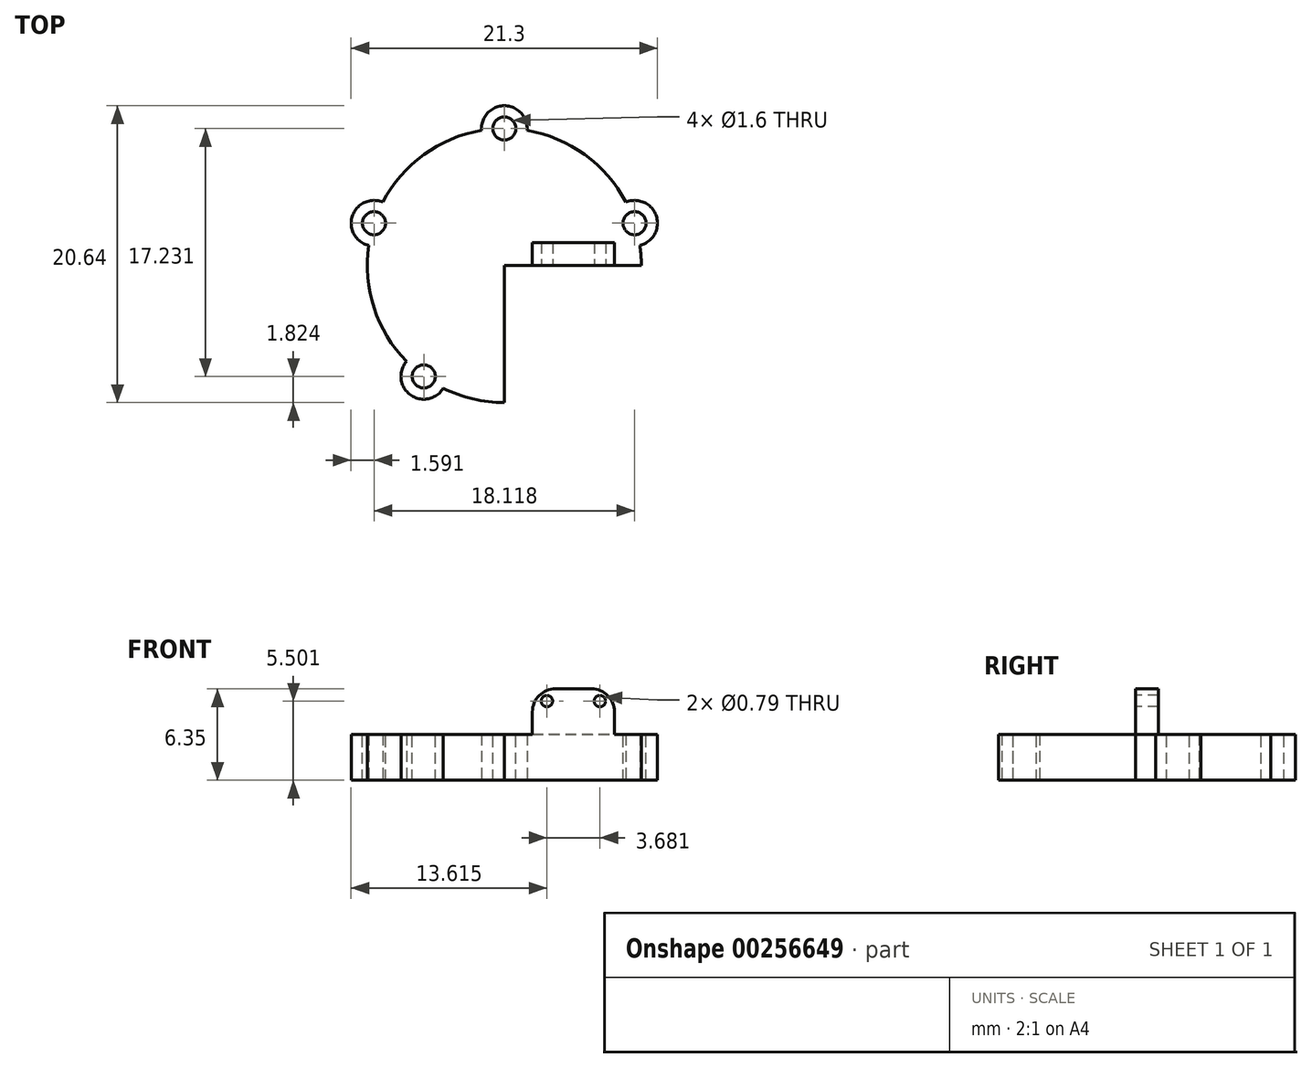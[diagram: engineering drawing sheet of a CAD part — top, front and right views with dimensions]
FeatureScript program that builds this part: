
annotation { "Feature Type Name" : "Feature", "Feature Type Description" : "" }
export const myFeature = defineFeature(function(context is Context, id is Id, definition is map)
    precondition{}
    {
        {
            var Q0;
            Q0=qCreatedBy(makeId("Top.planeOp"),FACE);
            var sketch = newSketch(context, id + "F0", { "sketchPlane" : qUnion([Q0])});
            skCircle(sketch, "E0", {"center": v(0, 0) * mm, "radius": 9.53 * mm});
            skSolve(sketch);
        }
        {
            var Q0;
            Q0=makeQuery(id+"F0.imprint","IMPRINT",FACE,{"disambiguationData":[TD([[makeQuery(id+"F0.imprint","IMPRINT",EDGE,{"derivedFrom":sQuery(id+"F0.wireOp",EDGE,"E0")}),1.0]])]});
            var sketch = newSketch(context, id + "F1", { "sketchPlane" : qUnion([Q0])});
            skCircle(sketch, "E1.0", {"center": v(0, 0) * mm, "radius": 9.53 * mm});
            skArc(sketch, "E2", {"start": v(1.58, 9.4) * mm, "mid": v(0, 11.11) * mm, "end": v(-1.58, 9.4) * mm});
            skCircle(sketch, "E3", {"center": v(0, 9.53) * mm, "radius": 0.8 * mm});
            skSolve(sketch);
        }
        {
            var Q0;
            Q0 = qSketchRegion(id + "F1", true);
            extrude(context, id + "F2", {"entities" : qUnion([Q0]), "depth" : 3.17 * mm});
        }
        {
            var Q0;
            Q0=qCreatedBy(makeId("Top.planeOp"),FACE);
            var sketch = newSketch(context, id + "F3", { "sketchPlane" : qUnion([Q0])});
            skArc(sketch, "E4.0", {"start": v(1.58, 9.4) * mm, "mid": v(0, 11.11) * mm, "end": v(-1.58, 9.4) * mm});
            skCircle(sketch, "E5.0", {"center": v(0, 9.53) * mm, "radius": 0.8 * mm});
            skArc(sketch, "E6.0", {"start": v(1.58, -9.4) * mm, "mid": v(0, 9.53) * mm, "end": v(-1.58, -9.4) * mm});
            skPoint(sketch, "E7.MirrorCS.end.orphan", {"position": v(-1.58, -9.4) * mm});
            skPoint(sketch, "E7.MirrorCS.start.orphan", {"position": v(1.58, -9.4) * mm});
            skArc(sketch, "E8.1.0", {"start": v(-8.44, 4.4) * mm, "mid": v(-10.57, 3.43) * mm, "end": v(-9.42, 1.4) * mm});
            skArc(sketch, "E8.2.0", {"start": v(-6.8, -6.67) * mm, "mid": v(-6.53, -9) * mm, "end": v(-4.24, -8.53) * mm});
            skArc(sketch, "E8.3.0", {"start": v(4.24, -8.53) * mm, "mid": v(6.53, -9) * mm, "end": v(6.8, -6.67) * mm});
            skArc(sketch, "E8.4.0", {"start": v(9.42, 1.4) * mm, "mid": v(10.57, 3.43) * mm, "end": v(8.44, 4.4) * mm});
            skCircle(sketch, "E9.1.0", {"center": v(-9.06, 2.94) * mm, "radius": 0.8 * mm});
            skCircle(sketch, "E9.2.0", {"center": v(-5.6, -7.7) * mm, "radius": 0.8 * mm});
            skCircle(sketch, "E9.3.0", {"center": v(5.6, -7.7) * mm, "radius": 0.8 * mm});
            skCircle(sketch, "E9.4.0", {"center": v(9.06, 2.94) * mm, "radius": 0.8 * mm});
            skSolve(sketch);
        }
        {
            var Q0;
            {var subQ0=sQuery(id+"F3.wireOp",EDGE,"E4.0");Q0=makeQuery(id+"F3.imprint","IMPRINT",FACE,{"disambiguationData":[TD([[makeQuery(id+"F3.imprint","IMPRINT",EDGE,{"derivedFrom":subQ0}),1.0]])]});}
            var Q1;
            {var subQ0=sQuery(id+"F3.wireOp",EDGE,"E6.0");var subQ1=sQuery(id+"F3.wireOp",EDGE,"E5.0");var subQ2=makeQuery(id+"F3.imprint","INTERSECT",VERTEX,{"disambiguationData":[OD(0.0)],"derivedFrom":[subQ1,subQ0]});Q1=makeQuery(id+"F3.imprint","IMPRINT",FACE,{"disambiguationData":[TD([[makeQuery(id+"F3.imprint","IMPRINT",EDGE,{"disambiguationData":[TD([[subQ2,1.0]])],"derivedFrom":subQ1}),1.0]])]});}
            var Q2;
            {var subQ0=sQuery(id+"F3.wireOp",EDGE,"E8.3.0");Q2=makeQuery(id+"F3.imprint","IMPRINT",FACE,{"disambiguationData":[TD([[makeQuery(id+"F3.imprint","IMPRINT",EDGE,{"derivedFrom":subQ0}),1.0]])]});}
            var Q3;
            {var subQ0=sQuery(id+"F3.wireOp",EDGE,"E9.3.0");var subQ1=sQuery(id+"F3.wireOp",EDGE,"E6.0");var subQ2=makeQuery(id+"F3.imprint","INTERSECT",VERTEX,{"disambiguationData":[OD(0.0)],"derivedFrom":[subQ1,subQ0]});Q3=makeQuery(id+"F3.imprint","IMPRINT",FACE,{"disambiguationData":[TD([[makeQuery(id+"F3.imprint","IMPRINT",EDGE,{"disambiguationData":[TD([[subQ2,-1.0]])],"derivedFrom":subQ1}),1.0]])]});}
            var Q4;
            {var subQ0=sQuery(id+"F3.wireOp",EDGE,"E8.4.0");Q4=makeQuery(id+"F3.imprint","IMPRINT",FACE,{"disambiguationData":[TD([[makeQuery(id+"F3.imprint","IMPRINT",EDGE,{"derivedFrom":subQ0}),1.0]])]});}
            var Q5;
            {var subQ0=sQuery(id+"F3.wireOp",EDGE,"E9.4.0");var subQ1=sQuery(id+"F3.wireOp",EDGE,"E6.0");var subQ2=makeQuery(id+"F3.imprint","INTERSECT",VERTEX,{"disambiguationData":[OD(0.0)],"derivedFrom":[subQ1,subQ0]});Q5=makeQuery(id+"F3.imprint","IMPRINT",FACE,{"disambiguationData":[TD([[makeQuery(id+"F3.imprint","IMPRINT",EDGE,{"disambiguationData":[TD([[subQ2,-1.0]])],"derivedFrom":subQ1}),1.0]])]});}
            var Q6;
            {var subQ0=sQuery(id+"F3.wireOp",EDGE,"E9.1.0");var subQ1=sQuery(id+"F3.wireOp",EDGE,"E6.0");var subQ2=makeQuery(id+"F3.imprint","INTERSECT",VERTEX,{"disambiguationData":[OD(0.0)],"derivedFrom":[subQ1,subQ0]});Q6=makeQuery(id+"F3.imprint","IMPRINT",FACE,{"disambiguationData":[TD([[makeQuery(id+"F3.imprint","IMPRINT",EDGE,{"disambiguationData":[TD([[subQ2,-1.0]])],"derivedFrom":subQ1}),1.0]])]});}
            var Q7;
            {var subQ0=sQuery(id+"F3.wireOp",EDGE,"E8.2.0");Q7=makeQuery(id+"F3.imprint","IMPRINT",FACE,{"disambiguationData":[TD([[makeQuery(id+"F3.imprint","IMPRINT",EDGE,{"derivedFrom":subQ0}),1.0]])]});}
            var Q8;
            {var subQ0=sQuery(id+"F3.wireOp",EDGE,"E9.2.0");var subQ1=sQuery(id+"F3.wireOp",EDGE,"E6.0");var subQ2=makeQuery(id+"F3.imprint","INTERSECT",VERTEX,{"disambiguationData":[OD(0.0)],"derivedFrom":[subQ1,subQ0]});Q8=makeQuery(id+"F3.imprint","IMPRINT",FACE,{"disambiguationData":[TD([[makeQuery(id+"F3.imprint","IMPRINT",EDGE,{"disambiguationData":[TD([[subQ2,-1.0]])],"derivedFrom":subQ1}),1.0]])]});}
            var Q9;
            {var subQ0=sQuery(id+"F3.wireOp",EDGE,"E6.0");var subQ1=sQuery(id+"F3.wireOp",EDGE,"E5.0");var subQ2=makeQuery(id+"F3.imprint","INTERSECT",VERTEX,{"disambiguationData":[OD(0.0)],"derivedFrom":[subQ1,subQ0]});Q9=makeQuery(id+"F3.imprint","IMPRINT",FACE,{"disambiguationData":[TD([[makeQuery(id+"F3.imprint","IMPRINT",EDGE,{"disambiguationData":[TD([[subQ2,-1.0]])],"derivedFrom":subQ1}),1.0]])]});}
            var Q10;
            {var subQ0=sQuery(id+"F3.wireOp",EDGE,"E9.3.0");var subQ1=sQuery(id+"F3.wireOp",EDGE,"E6.0");var subQ2=makeQuery(id+"F3.imprint","INTERSECT",VERTEX,{"disambiguationData":[OD(0.0)],"derivedFrom":[subQ1,subQ0]});Q10=makeQuery(id+"F3.imprint","IMPRINT",FACE,{"disambiguationData":[TD([[makeQuery(id+"F3.imprint","IMPRINT",EDGE,{"disambiguationData":[TD([[subQ2,-1.0]])],"derivedFrom":subQ1}),-1.0]])]});}
            var Q11;
            {var subQ0=sQuery(id+"F3.wireOp",EDGE,"E9.4.0");var subQ1=sQuery(id+"F3.wireOp",EDGE,"E6.0");var subQ2=makeQuery(id+"F3.imprint","INTERSECT",VERTEX,{"disambiguationData":[OD(0.0)],"derivedFrom":[subQ1,subQ0]});Q11=makeQuery(id+"F3.imprint","IMPRINT",FACE,{"disambiguationData":[TD([[makeQuery(id+"F3.imprint","IMPRINT",EDGE,{"disambiguationData":[TD([[subQ2,-1.0]])],"derivedFrom":subQ1}),-1.0]])]});}
            var Q12;
            {var subQ0=sQuery(id+"F3.wireOp",EDGE,"E9.1.0");var subQ1=sQuery(id+"F3.wireOp",EDGE,"E6.0");var subQ2=makeQuery(id+"F3.imprint","INTERSECT",VERTEX,{"disambiguationData":[OD(0.0)],"derivedFrom":[subQ1,subQ0]});Q12=makeQuery(id+"F3.imprint","IMPRINT",FACE,{"disambiguationData":[TD([[makeQuery(id+"F3.imprint","IMPRINT",EDGE,{"disambiguationData":[TD([[subQ2,-1.0]])],"derivedFrom":subQ1}),-1.0]])]});}
            var Q13;
            {var subQ0=sQuery(id+"F3.wireOp",EDGE,"E9.2.0");var subQ1=sQuery(id+"F3.wireOp",EDGE,"E6.0");var subQ2=makeQuery(id+"F3.imprint","INTERSECT",VERTEX,{"disambiguationData":[OD(0.0)],"derivedFrom":[subQ1,subQ0]});Q13=makeQuery(id+"F3.imprint","IMPRINT",FACE,{"disambiguationData":[TD([[makeQuery(id+"F3.imprint","IMPRINT",EDGE,{"disambiguationData":[TD([[subQ2,-1.0]])],"derivedFrom":subQ1}),-1.0]])]});}
            var Q14;
            {var subQ0=sQuery(id+"F3.wireOp",EDGE,"E8.1.0");Q14=makeQuery(id+"F3.imprint","IMPRINT",FACE,{"disambiguationData":[TD([[makeQuery(id+"F3.imprint","IMPRINT",EDGE,{"derivedFrom":subQ0}),1.0]])]});}
            extrude(context, id + "F4", {"entities" : qUnion([Q0, Q1, Q2, Q3, Q4, Q5, Q6, Q7, Q8, Q9, Q10, Q11, Q12, Q13, Q14]), "operationType" : NewBodyOperationType.ADD, "depth" : 3.17 * mm});
        }
        {
            var Q0;
            {var subQ0=sQuery(id+"F3.wireOp",EDGE,"E6.0");Q0=makeQuery(id+"F4.boolean.opBoolean","MERGE",FACE,{"derivedFrom":[makeQuery(id+"F2.opExtrude","CAP_FACE",FACE,{"disambiguationData":[OSD([sQuery(id+"F1.wireOp",EDGE,"E1.0"),sQuery(id+"F1.wireOp",EDGE,"E2"),sQuery(id+"F1.wireOp",EDGE,"E3")])],"isStart":false}),makeQuery(id+"F4.opExtrude","CAP_FACE",FACE,{"disambiguationData":[OSD([sQuery(id+"F3.wireOp",EDGE,"E4.0"),sQuery(id+"F3.wireOp",EDGE,"E5.0"),subQ0])],"isStart":false}),makeQuery(id+"F4.opExtrude","CAP_FACE",FACE,{"disambiguationData":[OSD([subQ0,sQuery(id+"F3.wireOp",EDGE,"E8.3.0"),sQuery(id+"F3.wireOp",EDGE,"E9.3.0")])],"isStart":false}),makeQuery(id+"F4.opExtrude","CAP_FACE",FACE,{"disambiguationData":[OSD([subQ0,sQuery(id+"F3.wireOp",EDGE,"E8.4.0"),sQuery(id+"F3.wireOp",EDGE,"E9.4.0")])],"isStart":false}),makeQuery(id+"F4.opExtrude","CAP_FACE",FACE,{"disambiguationData":[OSD([subQ0,sQuery(id+"F3.wireOp",EDGE,"E8.1.0"),sQuery(id+"F3.wireOp",EDGE,"E9.1.0")])],"isStart":false}),makeQuery(id+"F4.opExtrude","CAP_FACE",FACE,{"disambiguationData":[OSD([subQ0,sQuery(id+"F3.wireOp",EDGE,"E8.2.0"),sQuery(id+"F3.wireOp",EDGE,"E9.2.0")])],"isStart":false})]});}
            var sketch = newSketch(context, id + "F5", { "sketchPlane" : qUnion([Q0])});
            skCircle(sketch, "E10", {"center": v(0, 9.53) * mm, "radius": 0.8 * mm});
            skCircle(sketch, "E11.1.0", {"center": v(-9.06, 2.94) * mm, "radius": 0.8 * mm});
            skCircle(sketch, "E11.2.0", {"center": v(-5.6, -7.7) * mm, "radius": 0.8 * mm});
            skCircle(sketch, "E11.3.0", {"center": v(5.6, -7.7) * mm, "radius": 0.8 * mm});
            skCircle(sketch, "E11.4.0", {"center": v(9.06, 2.94) * mm, "radius": 0.8 * mm});
            skPoint(sketch, "E11.center", {"position": v(0, 0) * mm});
            skSolve(sketch);
        }
        {
            var Q0;
            Q0 = qSketchRegion(id + "F5", true);
            extrude(context, id + "F6", {"entities" : qUnion([Q0]), "operationType" : NewBodyOperationType.REMOVE, "oppositeDirection" : true, "depth" : 3.2 * mm});
        }
        {
            var Q0;
            {var subQ0=sQuery(id+"F3.wireOp",EDGE,"E6.0");Q0=makeQuery(id+"F4.boolean.opBoolean","MERGE",FACE,{"derivedFrom":[makeQuery(id+"F2.opExtrude","CAP_FACE",FACE,{"disambiguationData":[OSD([sQuery(id+"F1.wireOp",EDGE,"E1.0"),sQuery(id+"F1.wireOp",EDGE,"E2"),sQuery(id+"F1.wireOp",EDGE,"E3")])],"isStart":false}),makeQuery(id+"F4.opExtrude","CAP_FACE",FACE,{"disambiguationData":[OSD([sQuery(id+"F3.wireOp",EDGE,"E4.0"),sQuery(id+"F3.wireOp",EDGE,"E5.0"),subQ0])],"isStart":false}),makeQuery(id+"F4.opExtrude","CAP_FACE",FACE,{"disambiguationData":[OSD([subQ0,sQuery(id+"F3.wireOp",EDGE,"E8.3.0"),sQuery(id+"F3.wireOp",EDGE,"E9.3.0")])],"isStart":false}),makeQuery(id+"F4.opExtrude","CAP_FACE",FACE,{"disambiguationData":[OSD([subQ0,sQuery(id+"F3.wireOp",EDGE,"E8.4.0"),sQuery(id+"F3.wireOp",EDGE,"E9.4.0")])],"isStart":false}),makeQuery(id+"F4.opExtrude","CAP_FACE",FACE,{"disambiguationData":[OSD([subQ0,sQuery(id+"F3.wireOp",EDGE,"E8.1.0"),sQuery(id+"F3.wireOp",EDGE,"E9.1.0")])],"isStart":false}),makeQuery(id+"F4.opExtrude","CAP_FACE",FACE,{"disambiguationData":[OSD([subQ0,sQuery(id+"F3.wireOp",EDGE,"E8.2.0"),sQuery(id+"F3.wireOp",EDGE,"E9.2.0")])],"isStart":false})]});}
            var sketch = newSketch(context, id + "F7", { "sketchPlane" : qUnion([Q0])});
            skLineSegment(sketch, "E12", {"start": v(9.53, 0) * mm, "end": v(0, 0) * mm});
            skLineSegment(sketch, "E13", {"start": v(0, 0) * mm, "end": v(0, -9.53) * mm});
            skSolve(sketch);
        }
        {
            var Q0;
            Q0 = qSketchRegion(id + "F7", true);
            var Q1;
            {var subQ3=sQuery(id+"F7.wireOp",EDGE,"E12");Q1=makeQuery(id+"F7.imprint","IMPRINT",FACE,{"disambiguationData":[TD([[makeQuery(id+"F7.imprint","IMPRINT",EDGE,{"derivedFrom":subQ3}),1.0]])]});}
            extrude(context, id + "F8", {"entities" : qUnion([Q0, Q1]), "operationType" : NewBodyOperationType.REMOVE, "oppositeDirection" : true, "depth" : 25.4 * mm});
        }
        {
            var Q0;
            {var subQ0=sQuery(id+"F3.wireOp",EDGE,"E6.0");Q0=makeQuery(id+"F4.boolean.opBoolean","MERGE",FACE,{"derivedFrom":[makeQuery(id+"F2.opExtrude","CAP_FACE",FACE,{"disambiguationData":[OSD([sQuery(id+"F1.wireOp",EDGE,"E1.0"),sQuery(id+"F1.wireOp",EDGE,"E2"),sQuery(id+"F1.wireOp",EDGE,"E3")])],"isStart":false}),makeQuery(id+"F4.opExtrude","CAP_FACE",FACE,{"disambiguationData":[OSD([sQuery(id+"F3.wireOp",EDGE,"E4.0"),sQuery(id+"F3.wireOp",EDGE,"E5.0"),subQ0])],"isStart":false}),makeQuery(id+"F4.opExtrude","CAP_FACE",FACE,{"disambiguationData":[OSD([subQ0,sQuery(id+"F3.wireOp",EDGE,"E8.3.0"),sQuery(id+"F3.wireOp",EDGE,"E9.3.0")])],"isStart":false}),makeQuery(id+"F4.opExtrude","CAP_FACE",FACE,{"disambiguationData":[OSD([subQ0,sQuery(id+"F3.wireOp",EDGE,"E8.4.0"),sQuery(id+"F3.wireOp",EDGE,"E9.4.0")])],"isStart":false}),makeQuery(id+"F4.opExtrude","CAP_FACE",FACE,{"disambiguationData":[OSD([subQ0,sQuery(id+"F3.wireOp",EDGE,"E8.1.0"),sQuery(id+"F3.wireOp",EDGE,"E9.1.0")])],"isStart":false}),makeQuery(id+"F4.opExtrude","CAP_FACE",FACE,{"disambiguationData":[OSD([subQ0,sQuery(id+"F3.wireOp",EDGE,"E8.2.0"),sQuery(id+"F3.wireOp",EDGE,"E9.2.0")])],"isStart":false})]});}
            var sketch = newSketch(context, id + "F9", { "sketchPlane" : qUnion([Q0])});
            skLineSegment(sketch, "E14.0", {"start": v(7.66, 0) * mm, "end": v(1.95, 0) * mm});
            skArc(sketch, "E15.0", {"start": v(9.53, 0) * mm, "mid": v(-6.15, 7.27) * mm, "end": v(-1.58, -9.4) * mm});
            skArc(sketch, "E16.0", {"start": v(9.53, 0) * mm, "mid": v(-7.27, 6.15) * mm, "end": v(1.58, -9.4) * mm});
            skLineSegment(sketch, "E17", {"start": v(7.66, 0) * mm, "end": v(7.66, 1.6) * mm});
            skLineSegment(sketch, "E18", {"start": v(1.95, 0) * mm, "end": v(1.95, 1.6) * mm});
            skLineSegment(sketch, "E19", {"start": v(1.95, 1.6) * mm, "end": v(7.66, 1.6) * mm});
            skPoint(sketch, "E20.0.end.orphan", {"position": v(0, -9.53) * mm});
            skPoint(sketch, "E21.orphan", {"position": v(9.53, 0) * mm});
            skSolve(sketch);
        }
        {
            var Q0;
            Q0=makeQuery(id+"F9.imprint","IMPRINT",FACE,{"disambiguationData":[TD([[makeQuery(id+"F9.imprint","IMPRINT",EDGE,{"derivedFrom":sQuery(id+"F9.wireOp",EDGE,"E14.0")}),-1.0]])]});
            extrude(context, id + "F10", {"entities" : qUnion([Q0]), "operationType" : NewBodyOperationType.ADD, "depth" : 3.17 * mm});
        }
        {
            var Q0;
            Q0=makeQuery(id+"F10.boolean.opBoolean","MERGE",FACE,{"derivedFrom":[makeQuery(id+"F8.boolean.opBoolean","COPY",FACE,{"derivedFrom":makeQuery(id+"F8.opExtrude","SWEPT_FACE",FACE,{"disambiguationData":[OSD([sQuery(id+"F7.wireOp",EDGE,"E12")])]})}),makeQuery(id+"F10.opExtrude","SWEPT_FACE",FACE,{"disambiguationData":[OSD([sQuery(id+"F9.wireOp",EDGE,"E14.0")])]})]});
            var sketch = newSketch(context, id + "F11", { "sketchPlane" : qUnion([Q0])});
            skLineSegment(sketch, "E22.0", {"start": v(1.95, 4.75) * mm, "end": v(1.95, 3.18) * mm});
            skLineSegment(sketch, "E23.0", {"start": v(6.06, 6.35) * mm, "end": v(3.55, 6.35) * mm});
            skLineSegment(sketch, "E24.0", {"start": v(7.66, 4.75) * mm, "end": v(7.66, 3.18) * mm});
            skPoint(sketch, "E25.visualSharp", {"position": v(1.95, 6.35) * mm});
            skArc(sketch, "E25.filletArc", {"start": v(3.55, 6.35) * mm, "mid": v(2.42, 5.88) * mm, "end": v(1.95, 4.75) * mm});
            skPoint(sketch, "E26.visualSharp", {"position": v(7.66, 6.35) * mm});
            skArc(sketch, "E26.filletArc", {"start": v(7.66, 4.75) * mm, "mid": v(7.2, 5.88) * mm, "end": v(6.06, 6.35) * mm});
            skPoint(sketch, "E27.endSnap0", {"position": v(4.8, 6.35) * mm});
            skSolve(sketch);
        }
        {
            var Q0;
            Q0 = qSketchRegion(id + "F11", true);
            var Q1;
            {var subQ0=sQuery(id+"F11.wireOp",EDGE,"E25.filletArc");Q1=makeQuery(id+"F11.imprint","IMPRINT",FACE,{"disambiguationData":[TD([[makeQuery(id+"F11.imprint","IMPRINT",EDGE,{"derivedFrom":subQ0}),-1.0]])]});}
            var Q2;
            {var subQ0=sQuery(id+"F11.wireOp",EDGE,"E26.filletArc");Q2=makeQuery(id+"F11.imprint","IMPRINT",FACE,{"disambiguationData":[TD([[makeQuery(id+"F11.imprint","IMPRINT",EDGE,{"derivedFrom":subQ0}),-1.0]])]});}
            extrude(context, id + "F12", {"entities" : qUnion([Q0, Q1, Q2]), "operationType" : NewBodyOperationType.REMOVE, "oppositeDirection" : true, "depth" : 25.4 * mm});
        }
        {
            var Q0;
            Q0=makeQuery(id+"F10.boolean.opBoolean","MERGE",FACE,{"derivedFrom":[makeQuery(id+"F8.boolean.opBoolean","COPY",FACE,{"derivedFrom":makeQuery(id+"F8.opExtrude","SWEPT_FACE",FACE,{"disambiguationData":[OSD([sQuery(id+"F7.wireOp",EDGE,"E12")])]})}),makeQuery(id+"F10.opExtrude","SWEPT_FACE",FACE,{"disambiguationData":[OSD([sQuery(id+"F9.wireOp",EDGE,"E14.0")])]})]});
            var sketch = newSketch(context, id + "F13", { "sketchPlane" : qUnion([Q0])});
            skCircle(sketch, "E28", {"center": v(6.65, 5.5) * mm, "radius": 0.4 * mm});
            skLineSegment(sketch, "E29", {"start": v(4.8, 6.35) * mm, "end": v(4.8, 0) * mm, "construction": true});
            skCircle(sketch, "E30.MirrorC", {"center": v(2.96, 5.5) * mm, "radius": 0.4 * mm});
            skSolve(sketch);
        }
        {
            var Q0;
            Q0 = qSketchRegion(id + "F13", true);
            extrude(context, id + "F14", {"entities" : qUnion([Q0]), "operationType" : NewBodyOperationType.REMOVE, "oppositeDirection" : true, "depth" : 25.4 * mm});
        }
    });
